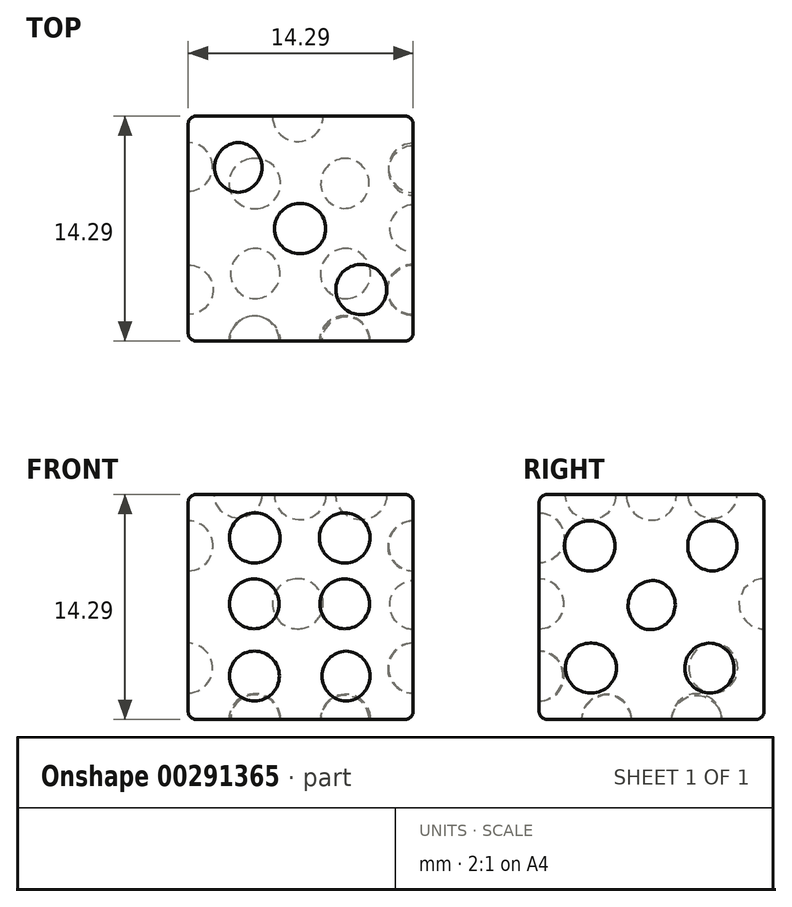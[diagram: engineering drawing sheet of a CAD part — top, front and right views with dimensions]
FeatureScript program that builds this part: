
annotation { "Feature Type Name" : "Feature", "Feature Type Description" : "" }
export const myFeature = defineFeature(function(context is Context, id is Id, definition is map)
    precondition{}
    {
        {
            var Q0;
            Q0=qCreatedBy(makeId("Front.planeOp"),FACE);
            var sketch = newSketch(context, id + "F0", { "sketchPlane" : qUnion([Q0])});
            skLineSegment(sketch, "E0.bottom", {"start": v(0, 0) * mm, "end": v(-14.29, 0) * mm});
            skLineSegment(sketch, "E0.top", {"start": v(0, 14.29) * mm, "end": v(-14.29, 14.29) * mm});
            skLineSegment(sketch, "E0.left", {"start": v(0, 0) * mm, "end": v(0, 14.29) * mm});
            skLineSegment(sketch, "E0.right", {"start": v(-14.29, 0) * mm, "end": v(-14.29, 14.29) * mm});
            skSolve(sketch);
        }
        {
            var Q0;
            Q0 = qSketchRegion(id + "F0", true);
            extrude(context, id + "F1", {"entities" : qUnion([Q0]), "depth" : 14.29 * mm});
        }
        {
            var Q0;
            Q0=makeQuery(id+"F1.opExtrude","CAP_FACE",FACE,{"disambiguationData":[OSD([sQuery(id+"F0.wireOp",EDGE,"E0.bottom"),sQuery(id+"F0.wireOp",EDGE,"E0.top"),sQuery(id+"F0.wireOp",EDGE,"E0.left"),sQuery(id+"F0.wireOp",EDGE,"E0.right")])],"isStart":false});
            var sketch = newSketch(context, id + "F2", { "sketchPlane" : qUnion([Q0])});
            skArc(sketch, "E1", {"start": v(-10.08, 4.34) * mm, "mid": v(-11.67, 2.76) * mm, "end": v(-10.08, 1.17) * mm});
            skLineSegment(sketch, "E2", {"start": v(-10.08, 4.34) * mm, "end": v(-10.08, 1.17) * mm});
            skLineSegment(sketch, "E3", {"start": v(-10.08, 1.17) * mm, "end": v(-10.08, 4.34) * mm});
            skSolve(sketch);
        }
        {
            var Q0;
            Q0 = qSketchRegion(id + "F2", true);
            var Q1;
            Q1=sQuery(id+"F2.wireOp",EDGE,"E3");
            revolve(context, id + "F3", {"operationType" : NewBodyOperationType.REMOVE, "entities" : qUnion([Q0]), "axis" : qUnion([Q1]), "revolveType" : RevolveType.FULL, "oppositeDirection" : true});
        }
        {
            var Q0;
            Q0=makeQuery(id+"F1.opExtrude","CAP_EDGE",EDGE,{"disambiguationData":[OSD([sQuery(id+"F0.wireOp",EDGE,"E0.top")])],"isStart":false});
            var Q1;
            Q1=makeQuery(id+"F1.opExtrude","SWEPT_EDGE",EDGE,{"disambiguationData":[OSD([sQuery(id+"F0.wireOp",EDGE,"E0.top"),sQuery(id+"F0.wireOp",EDGE,"E0.right")])]});
            var Q2;
            Q2=makeQuery(id+"F1.opExtrude","CAP_EDGE",EDGE,{"disambiguationData":[OSD([sQuery(id+"F0.wireOp",EDGE,"E0.right")])],"isStart":false});
            var Q3;
            Q3=makeQuery(id+"F1.opExtrude","SWEPT_EDGE",EDGE,{"disambiguationData":[OSD([sQuery(id+"F0.wireOp",EDGE,"E0.bottom"),sQuery(id+"F0.wireOp",EDGE,"E0.right")])]});
            var Q4;
            Q4=makeQuery(id+"F1.opExtrude","CAP_EDGE",EDGE,{"disambiguationData":[OSD([sQuery(id+"F0.wireOp",EDGE,"E0.bottom")])],"isStart":false});
            var Q5;
            Q5=makeQuery(id+"F1.opExtrude","CAP_EDGE",EDGE,{"disambiguationData":[OSD([sQuery(id+"F0.wireOp",EDGE,"E0.left")])],"isStart":false});
            var Q6;
            Q6=makeQuery(id+"F1.opExtrude","SWEPT_EDGE",EDGE,{"disambiguationData":[OSD([sQuery(id+"F0.wireOp",EDGE,"E0.top"),sQuery(id+"F0.wireOp",EDGE,"E0.left")])]});
            var Q7;
            Q7=makeQuery(id+"F1.opExtrude","CAP_EDGE",EDGE,{"disambiguationData":[OSD([sQuery(id+"F0.wireOp",EDGE,"E0.top")])],"isStart":true});
            var Q8;
            Q8=makeQuery(id+"F1.opExtrude","CAP_EDGE",EDGE,{"disambiguationData":[OSD([sQuery(id+"F0.wireOp",EDGE,"E0.right")])],"isStart":true});
            var Q9;
            Q9=makeQuery(id+"F1.opExtrude","CAP_EDGE",EDGE,{"disambiguationData":[OSD([sQuery(id+"F0.wireOp",EDGE,"E0.left")])],"isStart":true});
            var Q10;
            Q10=makeQuery(id+"F1.opExtrude","SWEPT_EDGE",EDGE,{"disambiguationData":[OSD([sQuery(id+"F0.wireOp",EDGE,"E0.bottom"),sQuery(id+"F0.wireOp",EDGE,"E0.left")])]});
            var Q11;
            Q11=makeQuery(id+"F1.opExtrude","CAP_EDGE",EDGE,{"disambiguationData":[OSD([sQuery(id+"F0.wireOp",EDGE,"E0.bottom")])],"isStart":true});
            fillet(context, id + "F4", {"entities" : qUnion([Q0, Q1, Q2, Q3, Q4, Q5, Q6, Q7, Q8, Q9, Q10, Q11]), "radius" : 0.5 * mm, "tangentPropagation" : true, "allowEdgeOverflow" : false});
        }
        {
            var Q0;
            Q0=makeQuery(id+"F1.opExtrude","CAP_FACE",FACE,{"disambiguationData":[OSD([sQuery(id+"F0.wireOp",EDGE,"E0.bottom"),sQuery(id+"F0.wireOp",EDGE,"E0.top"),sQuery(id+"F0.wireOp",EDGE,"E0.left"),sQuery(id+"F0.wireOp",EDGE,"E0.right")])],"isStart":false});
            var sketch = newSketch(context, id + "F5", { "sketchPlane" : qUnion([Q0])});
            skArc(sketch, "E4", {"start": v(-10.04, 13.12) * mm, "mid": v(-11.67, 11.55) * mm, "end": v(-10.08, 9.94) * mm});
            skLineSegment(sketch, "E5", {"start": v(-10.04, 13.12) * mm, "end": v(-10.08, 9.94) * mm});
            skLineSegment(sketch, "E6", {"start": v(-10.08, 9.94) * mm, "end": v(-10.04, 13.12) * mm});
            skSolve(sketch);
        }
        {
            var Q0;
            Q0 = qSketchRegion(id + "F5", true);
            var Q1;
            Q1=sQuery(id+"F5.wireOp",EDGE,"E6");
            revolve(context, id + "F6", {"operationType" : NewBodyOperationType.REMOVE, "entities" : qUnion([Q0]), "axis" : qUnion([Q1]), "revolveType" : RevolveType.FULL, "oppositeDirection" : true});
        }
        {
            var Q0;
            Q0=makeQuery(id+"F1.opExtrude","CAP_FACE",FACE,{"disambiguationData":[OSD([sQuery(id+"F0.wireOp",EDGE,"E0.bottom"),sQuery(id+"F0.wireOp",EDGE,"E0.top"),sQuery(id+"F0.wireOp",EDGE,"E0.left"),sQuery(id+"F0.wireOp",EDGE,"E0.right")])],"isStart":false});
            var sketch = newSketch(context, id + "F7", { "sketchPlane" : qUnion([Q0])});
            skArc(sketch, "E7", {"start": v(-10.1, 8.93) * mm, "mid": v(-11.67, 7.35) * mm, "end": v(-10.1, 5.76) * mm});
            skLineSegment(sketch, "E8", {"start": v(-10.1, 8.93) * mm, "end": v(-10.1, 5.76) * mm});
            skLineSegment(sketch, "E9", {"start": v(-10.1, 5.76) * mm, "end": v(-10.1, 8.93) * mm});
            skSolve(sketch);
        }
        {
            var Q0;
            Q0 = qSketchRegion(id + "F7", true);
            var Q1;
            Q1=sQuery(id+"F7.wireOp",EDGE,"E8");
            revolve(context, id + "F8", {"operationType" : NewBodyOperationType.REMOVE, "entities" : qUnion([Q0]), "axis" : qUnion([Q1]), "revolveType" : RevolveType.FULL, "oppositeDirection" : true});
        }
        {
            var Q0;
            Q0=makeQuery(id+"F1.opExtrude","CAP_FACE",FACE,{"disambiguationData":[OSD([sQuery(id+"F0.wireOp",EDGE,"E0.bottom"),sQuery(id+"F0.wireOp",EDGE,"E0.top"),sQuery(id+"F0.wireOp",EDGE,"E0.left"),sQuery(id+"F0.wireOp",EDGE,"E0.right")])],"isStart":false});
            var sketch = newSketch(context, id + "F9", { "sketchPlane" : qUnion([Q0])});
            skArc(sketch, "E10", {"start": v(-4.33, 9.94) * mm, "mid": v(-2.74, 11.55) * mm, "end": v(-4.37, 13.12) * mm});
            skLineSegment(sketch, "E11", {"start": v(-4.37, 13.12) * mm, "end": v(-4.33, 9.94) * mm});
            skLineSegment(sketch, "E12", {"start": v(-4.33, 9.94) * mm, "end": v(-4.37, 13.12) * mm});
            skSolve(sketch);
        }
        {
            var Q0;
            Q0 = qSketchRegion(id + "F9", true);
            var Q1;
            Q1=sQuery(id+"F9.wireOp",EDGE,"E12");
            revolve(context, id + "F10", {"operationType" : NewBodyOperationType.REMOVE, "entities" : qUnion([Q0]), "axis" : qUnion([Q1]), "revolveType" : RevolveType.FULL, "oppositeDirection" : true});
        }
        {
            var Q0;
            Q0=makeQuery(id+"F1.opExtrude","CAP_FACE",FACE,{"disambiguationData":[OSD([sQuery(id+"F0.wireOp",EDGE,"E0.bottom"),sQuery(id+"F0.wireOp",EDGE,"E0.top"),sQuery(id+"F0.wireOp",EDGE,"E0.left"),sQuery(id+"F0.wireOp",EDGE,"E0.right")])],"isStart":false});
            var sketch = newSketch(context, id + "F11", { "sketchPlane" : qUnion([Q0])});
            skArc(sketch, "E13", {"start": v(-4.35, 8.93) * mm, "mid": v(-5.92, 7.35) * mm, "end": v(-4.35, 5.76) * mm});
            skLineSegment(sketch, "E14", {"start": v(-4.35, 8.93) * mm, "end": v(-4.35, 5.76) * mm});
            skLineSegment(sketch, "E15", {"start": v(-4.35, 5.76) * mm, "end": v(-4.35, 8.93) * mm});
            skSolve(sketch);
        }
        {
            var Q0;
            Q0 = qSketchRegion(id + "F11", true);
            var Q1;
            Q1=sQuery(id+"F11.wireOp",EDGE,"E15");
            revolve(context, id + "F12", {"operationType" : NewBodyOperationType.REMOVE, "entities" : qUnion([Q0]), "axis" : qUnion([Q1]), "revolveType" : RevolveType.FULL, "oppositeDirection" : true});
        }
        {
            var Q0;
            Q0=makeQuery(id+"F1.opExtrude","CAP_FACE",FACE,{"disambiguationData":[OSD([sQuery(id+"F0.wireOp",EDGE,"E0.bottom"),sQuery(id+"F0.wireOp",EDGE,"E0.top"),sQuery(id+"F0.wireOp",EDGE,"E0.left"),sQuery(id+"F0.wireOp",EDGE,"E0.right")])],"isStart":false});
            var sketch = newSketch(context, id + "F13", { "sketchPlane" : qUnion([Q0])});
            skArc(sketch, "E16", {"start": v(-4.26, 4.34) * mm, "mid": v(-5.8, 2.76) * mm, "end": v(-4.26, 1.17) * mm});
            skLineSegment(sketch, "E17", {"start": v(-4.26, 4.34) * mm, "end": v(-4.26, 1.17) * mm});
            skLineSegment(sketch, "E18", {"start": v(-4.26, 1.17) * mm, "end": v(-4.26, 4.34) * mm});
            skSolve(sketch);
        }
        {
            var Q0;
            Q0 = qSketchRegion(id + "F13", true);
            var Q1;
            Q1=sQuery(id+"F13.wireOp",EDGE,"E18");
            revolve(context, id + "F14", {"operationType" : NewBodyOperationType.REMOVE, "entities" : qUnion([Q0]), "axis" : qUnion([Q1]), "revolveType" : RevolveType.FULL, "oppositeDirection" : true});
        }
        {
            var Q0;
            Q0=makeQuery(id+"F1.opExtrude","CAP_FACE",FACE,{"disambiguationData":[OSD([sQuery(id+"F0.wireOp",EDGE,"E0.bottom"),sQuery(id+"F0.wireOp",EDGE,"E0.top"),sQuery(id+"F0.wireOp",EDGE,"E0.left"),sQuery(id+"F0.wireOp",EDGE,"E0.right")])],"isStart":true});
            var sketch = newSketch(context, id + "F15", { "sketchPlane" : qUnion([Q0])});
            skArc(sketch, "E19", {"start": v(7.35, 5.76) * mm, "mid": v(8.94, 7.37) * mm, "end": v(7.3, 8.93) * mm});
            skLineSegment(sketch, "E20", {"start": v(7.3, 8.93) * mm, "end": v(7.35, 5.76) * mm});
            skLineSegment(sketch, "E21", {"start": v(7.35, 5.76) * mm, "end": v(7.3, 8.93) * mm});
            skSolve(sketch);
        }
        {
            var Q0;
            Q0 = qSketchRegion(id + "F15", true);
            var Q1;
            Q1=sQuery(id+"F15.wireOp",EDGE,"E21");
            revolve(context, id + "F16", {"operationType" : NewBodyOperationType.REMOVE, "entities" : qUnion([Q0]), "axis" : qUnion([Q1]), "revolveType" : RevolveType.FULL, "oppositeDirection" : true});
        }
        {
            var Q0;
            Q0=makeQuery(id+"F1.opExtrude","SWEPT_FACE",FACE,{"disambiguationData":[OSD([sQuery(id+"F0.wireOp",EDGE,"E0.left")])]});
            var sketch = newSketch(context, id + "F17", { "sketchPlane" : qUnion([Q0])});
            skArc(sketch, "E22", {"start": v(-6.67, 8.78) * mm, "mid": v(-8.57, 7.7) * mm, "end": v(-7.6, 5.75) * mm});
            skLineSegment(sketch, "E23", {"start": v(-6.67, 8.78) * mm, "end": v(-7.6, 5.75) * mm});
            skLineSegment(sketch, "E24", {"start": v(-7.6, 5.75) * mm, "end": v(-6.67, 8.78) * mm});
            skSolve(sketch);
        }
        {
            var Q0;
            Q0 = qSketchRegion(id + "F17", true);
            var Q1;
            Q1=sQuery(id+"F17.wireOp",EDGE,"E24");
            revolve(context, id + "F18", {"operationType" : NewBodyOperationType.REMOVE, "entities" : qUnion([Q0]), "axis" : qUnion([Q1]), "revolveType" : RevolveType.FULL, "oppositeDirection" : true});
        }
        {
            var Q0;
            Q0=makeQuery(id+"F1.opExtrude","SWEPT_FACE",FACE,{"disambiguationData":[OSD([sQuery(id+"F0.wireOp",EDGE,"E0.left")])]});
            var sketch = newSketch(context, id + "F19", { "sketchPlane" : qUnion([Q0])});
            skArc(sketch, "E25", {"start": v(-11.07, 12.61) * mm, "mid": v(-12.69, 11.02) * mm, "end": v(-11.07, 9.44) * mm});
            skLineSegment(sketch, "E26", {"start": v(-11.07, 9.44) * mm, "end": v(-11.07, 12.61) * mm});
            skLineSegment(sketch, "E27", {"start": v(-11.07, 12.61) * mm, "end": v(-11.07, 9.44) * mm});
            skSolve(sketch);
        }
        {
            var Q0;
            Q0 = qSketchRegion(id + "F19", true);
            var Q1;
            Q1=sQuery(id+"F19.wireOp",EDGE,"E26");
            revolve(context, id + "F20", {"operationType" : NewBodyOperationType.REMOVE, "entities" : qUnion([Q0]), "axis" : qUnion([Q1]), "revolveType" : RevolveType.FULL, "oppositeDirection" : true});
        }
        {
            var Q0;
            Q0=makeQuery(id+"F1.opExtrude","SWEPT_FACE",FACE,{"disambiguationData":[OSD([sQuery(id+"F0.wireOp",EDGE,"E0.left")])]});
            var sketch = newSketch(context, id + "F21", { "sketchPlane" : qUnion([Q0])});
            skArc(sketch, "E28", {"start": v(-3.48, 4.85) * mm, "mid": v(-5.03, 3.24) * mm, "end": v(-3.44, 1.68) * mm});
            skLineSegment(sketch, "E29", {"start": v(-3.48, 4.85) * mm, "end": v(-3.44, 1.68) * mm});
            skLineSegment(sketch, "E30", {"start": v(-3.44, 1.68) * mm, "end": v(-3.48, 4.85) * mm});
            skSolve(sketch);
        }
        {
            var Q0;
            Q0 = qSketchRegion(id + "F21", true);
            var Q1;
            Q1=sQuery(id+"F21.wireOp",EDGE,"E30");
            revolve(context, id + "F22", {"operationType" : NewBodyOperationType.REMOVE, "entities" : qUnion([Q0]), "axis" : qUnion([Q1]), "revolveType" : RevolveType.FULL, "oppositeDirection" : true});
        }
        {
            var Q0;
            Q0=makeQuery(id+"F1.opExtrude","SWEPT_FACE",FACE,{"disambiguationData":[OSD([sQuery(id+"F0.wireOp",EDGE,"E0.left")])]});
            var sketch = newSketch(context, id + "F23", { "sketchPlane" : qUnion([Q0])});
            skArc(sketch, "E31", {"start": v(-11, 4.85) * mm, "mid": v(-12.61, 3.26) * mm, "end": v(-11, 1.68) * mm});
            skLineSegment(sketch, "E32", {"start": v(-11, 4.85) * mm, "end": v(-11, 1.68) * mm});
            skLineSegment(sketch, "E33", {"start": v(-11, 1.68) * mm, "end": v(-11, 4.85) * mm});
            skSolve(sketch);
        }
        {
            var Q0;
            Q0 = qSketchRegion(id + "F23", true);
            var Q1;
            Q1=sQuery(id+"F23.wireOp",EDGE,"E33");
            revolve(context, id + "F24", {"operationType" : NewBodyOperationType.REMOVE, "entities" : qUnion([Q0]), "axis" : qUnion([Q1]), "revolveType" : RevolveType.FULL, "oppositeDirection" : true});
        }
        {
            var Q0;
            Q0=makeQuery(id+"F1.opExtrude","SWEPT_FACE",FACE,{"disambiguationData":[OSD([sQuery(id+"F0.wireOp",EDGE,"E0.left")])]});
            var sketch = newSketch(context, id + "F25", { "sketchPlane" : qUnion([Q0])});
            skArc(sketch, "E34", {"start": v(-3.3, 12.61) * mm, "mid": v(-4.85, 11.02) * mm, "end": v(-3.3, 9.44) * mm});
            skLineSegment(sketch, "E35", {"start": v(-3.3, 12.61) * mm, "end": v(-3.3, 9.44) * mm});
            skLineSegment(sketch, "E36", {"start": v(-3.3, 9.44) * mm, "end": v(-3.3, 12.61) * mm});
            skSolve(sketch);
        }
        {
            var Q0;
            Q0 = qSketchRegion(id + "F25", true);
            var Q1;
            Q1=sQuery(id+"F25.wireOp",EDGE,"E36");
            revolve(context, id + "F26", {"operationType" : NewBodyOperationType.REMOVE, "entities" : qUnion([Q0]), "axis" : qUnion([Q1]), "revolveType" : RevolveType.FULL, "oppositeDirection" : true});
        }
        {
            var Q0;
            Q0=makeQuery(id+"F1.opExtrude","SWEPT_FACE",FACE,{"disambiguationData":[OSD([sQuery(id+"F0.wireOp",EDGE,"E0.right")])]});
            var sketch = newSketch(context, id + "F27", { "sketchPlane" : qUnion([Q0])});
            skArc(sketch, "E37", {"start": v(3.23, 4.85) * mm, "mid": v(1.68, 3.26) * mm, "end": v(3.23, 1.68) * mm});
            skLineSegment(sketch, "E38", {"start": v(3.23, 4.85) * mm, "end": v(3.23, 1.68) * mm});
            skLineSegment(sketch, "E39", {"start": v(3.23, 1.68) * mm, "end": v(3.23, 4.85) * mm});
            skSolve(sketch);
        }
        {
            var Q0;
            Q0 = qSketchRegion(id + "F27", true);
            var Q1;
            Q1=sQuery(id+"F27.wireOp",EDGE,"E39");
            revolve(context, id + "F28", {"operationType" : NewBodyOperationType.REMOVE, "entities" : qUnion([Q0]), "axis" : qUnion([Q1]), "revolveType" : RevolveType.FULL, "oppositeDirection" : true});
        }
        {
            var Q0;
            Q0=makeQuery(id+"F1.opExtrude","SWEPT_FACE",FACE,{"disambiguationData":[OSD([sQuery(id+"F0.wireOp",EDGE,"E0.right")])]});
            var sketch = newSketch(context, id + "F29", { "sketchPlane" : qUnion([Q0])});
            skArc(sketch, "E40", {"start": v(11.04, 9.44) * mm, "mid": v(12.61, 11.02) * mm, "end": v(11.04, 12.61) * mm});
            skLineSegment(sketch, "E41", {"start": v(11.04, 12.61) * mm, "end": v(11.04, 9.44) * mm});
            skLineSegment(sketch, "E42", {"start": v(11.04, 9.44) * mm, "end": v(11.04, 12.61) * mm});
            skSolve(sketch);
        }
        {
            var Q0;
            Q0 = qSketchRegion(id + "F29", true);
            var Q1;
            Q1=sQuery(id+"F29.wireOp",EDGE,"E42");
            revolve(context, id + "F30", {"operationType" : NewBodyOperationType.REMOVE, "entities" : qUnion([Q0]), "axis" : qUnion([Q1]), "revolveType" : RevolveType.FULL});
        }
        {
            var Q0;
            Q0=makeQuery(id+"F1.opExtrude","SWEPT_FACE",FACE,{"disambiguationData":[OSD([sQuery(id+"F0.wireOp",EDGE,"E0.top")])]});
            var sketch = newSketch(context, id + "F31", { "sketchPlane" : qUnion([Q0])});
            skArc(sketch, "E43", {"start": v(-11.1, -1.68) * mm, "mid": v(-12.61, -3.26) * mm, "end": v(-11.1, -4.85) * mm});
            skLineSegment(sketch, "E44", {"start": v(-11.1, -1.68) * mm, "end": v(-11.1, -4.85) * mm});
            skLineSegment(sketch, "E45", {"start": v(-11.1, -4.85) * mm, "end": v(-11.1, -1.68) * mm});
            skSolve(sketch);
        }
        {
            var Q0;
            Q0 = qSketchRegion(id + "F31", true);
            var Q1;
            Q1=sQuery(id+"F31.wireOp",EDGE,"E45");
            revolve(context, id + "F32", {"operationType" : NewBodyOperationType.REMOVE, "entities" : qUnion([Q0]), "axis" : qUnion([Q1]), "revolveType" : RevolveType.FULL, "oppositeDirection" : true});
        }
        {
            var Q0;
            Q0=makeQuery(id+"F1.opExtrude","SWEPT_FACE",FACE,{"disambiguationData":[OSD([sQuery(id+"F0.wireOp",EDGE,"E0.top")])]});
            var sketch = newSketch(context, id + "F33", { "sketchPlane" : qUnion([Q0])});
            skArc(sketch, "E46", {"start": v(-3.26, -12.61) * mm, "mid": v(-1.68, -11) * mm, "end": v(-3.32, -9.44) * mm});
            skLineSegment(sketch, "E47", {"start": v(-3.32, -9.44) * mm, "end": v(-3.26, -12.61) * mm});
            skLineSegment(sketch, "E48", {"start": v(-3.26, -12.61) * mm, "end": v(-3.32, -9.44) * mm});
            skSolve(sketch);
        }
        {
            var Q0;
            Q0 = qSketchRegion(id + "F33", true);
            var Q1;
            Q1=sQuery(id+"F33.wireOp",EDGE,"E47");
            revolve(context, id + "F34", {"operationType" : NewBodyOperationType.REMOVE, "entities" : qUnion([Q0]), "axis" : qUnion([Q1]), "revolveType" : RevolveType.FULL});
        }
        {
            var Q0;
            Q0=makeQuery(id+"F1.opExtrude","SWEPT_FACE",FACE,{"disambiguationData":[OSD([sQuery(id+"F0.wireOp",EDGE,"E0.top")])]});
            var sketch = newSketch(context, id + "F35", { "sketchPlane" : qUnion([Q0])});
            skArc(sketch, "E49", {"start": v(-7.18, -8.74) * mm, "mid": v(-5.55, -7.15) * mm, "end": v(-7.18, -5.56) * mm});
            skLineSegment(sketch, "E50", {"start": v(-7.18, -5.56) * mm, "end": v(-7.18, -8.74) * mm});
            skLineSegment(sketch, "E51", {"start": v(-7.18, -8.74) * mm, "end": v(-7.18, -5.56) * mm});
            skSolve(sketch);
        }
        {
            var Q0;
            Q0 = qSketchRegion(id + "F35", true);
            var Q1;
            Q1=sQuery(id+"F35.wireOp",EDGE,"E51");
            revolve(context, id + "F36", {"operationType" : NewBodyOperationType.REMOVE, "entities" : qUnion([Q0]), "axis" : qUnion([Q1]), "revolveType" : RevolveType.FULL, "oppositeDirection" : true});
        }
        {
            var Q0;
            Q0=makeQuery(id+"F1.opExtrude","SWEPT_FACE",FACE,{"disambiguationData":[OSD([sQuery(id+"F0.wireOp",EDGE,"E0.bottom")])]});
            var sketch = newSketch(context, id + "F37", { "sketchPlane" : qUnion([Q0])});
            skArc(sketch, "E52", {"start": v(-10.04, 11.6) * mm, "mid": v(-11.6, 10) * mm, "end": v(-10, 8.42) * mm});
            skLineSegment(sketch, "E53", {"start": v(-10.04, 11.6) * mm, "end": v(-10, 8.42) * mm});
            skLineSegment(sketch, "E54", {"start": v(-10, 8.42) * mm, "end": v(-10.04, 11.6) * mm});
            skSolve(sketch);
        }
        {
            var Q0;
            Q0 = qSketchRegion(id + "F37", true);
            var Q1;
            Q1=sQuery(id+"F37.wireOp",EDGE,"E53");
            revolve(context, id + "F38", {"operationType" : NewBodyOperationType.REMOVE, "entities" : qUnion([Q0]), "axis" : qUnion([Q1]), "revolveType" : RevolveType.FULL, "oppositeDirection" : true});
        }
        {
            var Q0;
            Q0=makeQuery(id+"F1.opExtrude","SWEPT_FACE",FACE,{"disambiguationData":[OSD([sQuery(id+"F0.wireOp",EDGE,"E0.bottom")])]});
            var sketch = newSketch(context, id + "F39", { "sketchPlane" : qUnion([Q0])});
            skArc(sketch, "E55", {"start": v(-4.28, 8.42) * mm, "mid": v(-2.7, 10.02) * mm, "end": v(-4.3, 11.6) * mm});
            skLineSegment(sketch, "E56", {"start": v(-4.3, 11.6) * mm, "end": v(-4.28, 8.42) * mm});
            skLineSegment(sketch, "E57", {"start": v(-4.28, 8.42) * mm, "end": v(-4.3, 11.6) * mm});
            skSolve(sketch);
        }
        {
            var Q0;
            Q0 = qSketchRegion(id + "F39", true);
            var Q1;
            Q1=sQuery(id+"F39.wireOp",EDGE,"E57");
            revolve(context, id + "F40", {"operationType" : NewBodyOperationType.REMOVE, "entities" : qUnion([Q0]), "axis" : qUnion([Q1]), "revolveType" : RevolveType.FULL, "oppositeDirection" : true});
        }
        {
            var Q0;
            Q0=makeQuery(id+"F1.opExtrude","SWEPT_FACE",FACE,{"disambiguationData":[OSD([sQuery(id+"F0.wireOp",EDGE,"E0.bottom")])]});
            var sketch = newSketch(context, id + "F41", { "sketchPlane" : qUnion([Q0])});
            skArc(sketch, "E58", {"start": v(-10.2, 2.7) * mm, "mid": v(-8.43, 4.13) * mm, "end": v(-9.91, 5.86) * mm});
            skLineSegment(sketch, "E59", {"start": v(-9.91, 5.86) * mm, "end": v(-10.2, 2.7) * mm});
            skLineSegment(sketch, "E60", {"start": v(-10.2, 2.7) * mm, "end": v(-9.91, 5.86) * mm});
            skSolve(sketch);
        }
        {
            var Q0;
            Q0 = qSketchRegion(id + "F41", true);
            var Q1;
            Q1=sQuery(id+"F41.wireOp",EDGE,"E59");
            revolve(context, id + "F42", {"operationType" : NewBodyOperationType.REMOVE, "entities" : qUnion([Q0]), "axis" : qUnion([Q1]), "revolveType" : RevolveType.FULL, "oppositeDirection" : true});
        }
        {
            var Q0;
            Q0=makeQuery(id+"F1.opExtrude","SWEPT_FACE",FACE,{"disambiguationData":[OSD([sQuery(id+"F0.wireOp",EDGE,"E0.bottom")])]});
            var sketch = newSketch(context, id + "F43", { "sketchPlane" : qUnion([Q0])});
            skArc(sketch, "E61", {"start": v(-4.4, 5.86) * mm, "mid": v(-5.87, 4.2) * mm, "end": v(-4.25, 2.7) * mm});
            skLineSegment(sketch, "E62", {"start": v(-4.4, 5.86) * mm, "end": v(-4.25, 2.7) * mm});
            skLineSegment(sketch, "E63", {"start": v(-4.25, 2.7) * mm, "end": v(-4.4, 5.86) * mm});
            skSolve(sketch);
        }
        {
            var Q0;
            Q0 = qSketchRegion(id + "F43", true);
            var Q1;
            Q1=sQuery(id+"F43.wireOp",EDGE,"E63");
            revolve(context, id + "F44", {"operationType" : NewBodyOperationType.REMOVE, "entities" : qUnion([Q0]), "axis" : qUnion([Q1]), "revolveType" : RevolveType.FULL, "oppositeDirection" : true});
        }
    });
